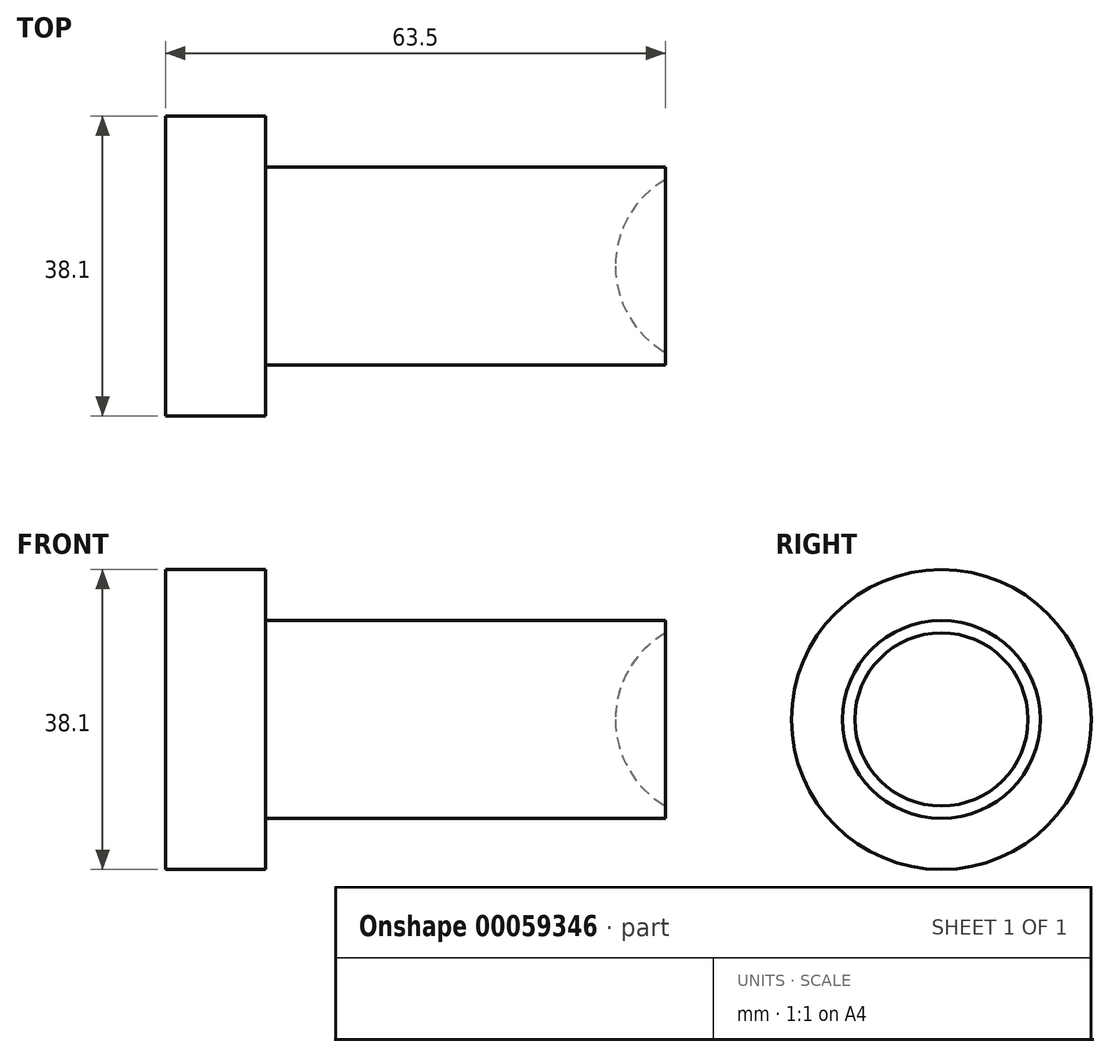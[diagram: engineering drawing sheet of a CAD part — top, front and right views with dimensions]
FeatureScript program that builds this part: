
annotation { "Feature Type Name" : "Feature", "Feature Type Description" : "" }
export const myFeature = defineFeature(function(context is Context, id is Id, definition is map)
    precondition{}
    {
        {
            var Q0;
            Q0=qCreatedBy(makeId("Front.planeOp"),FACE);
            var sketch = newSketch(context, id + "F0", { "sketchPlane" : qUnion([Q0])});
            skLineSegment(sketch, "E0", {"start": v(-12.7, 0) * mm, "end": v(-12.7, 19.05) * mm});
            skLineSegment(sketch, "E1", {"start": v(-12.7, 19.05) * mm, "end": v(0, 19.05) * mm});
            skLineSegment(sketch, "E2", {"start": v(0, 19.05) * mm, "end": v(0, 12.57) * mm});
            skLineSegment(sketch, "E3", {"start": v(-12.7, 0) * mm, "end": v(44.45, 0) * mm});
            skLineSegment(sketch, "E4", {"start": v(50.8, 11) * mm, "end": v(50.8, 12.57) * mm});
            skLineSegment(sketch, "E5", {"start": v(50.8, 12.57) * mm, "end": v(0, 12.57) * mm});
            skPoint(sketch, "E6.orphan", {"position": v(0, 0) * mm});
            skLineSegment(sketch, "E7", {"start": v(-21.1, 0) * mm, "end": v(29.59, 0) * mm, "construction": true});
            skArc(sketch, "E8", {"start": v(50.8, 11) * mm, "mid": v(46.15, 6.35) * mm, "end": v(44.45, 0) * mm});
            skPoint(sketch, "E9.orphan", {"position": v(50.8, 0) * mm});
            skSolve(sketch);
        }
        {
            var Q0;
            Q0 = qSketchRegion(id + "F0", true);
            var Q1;
            Q1=sQuery(id+"F0.wireOp",EDGE,"E3");
            revolve(context, id + "F1", {"entities" : qUnion([Q0]), "axis" : qUnion([Q1]), "revolveType" : RevolveType.FULL});
        }
    });
